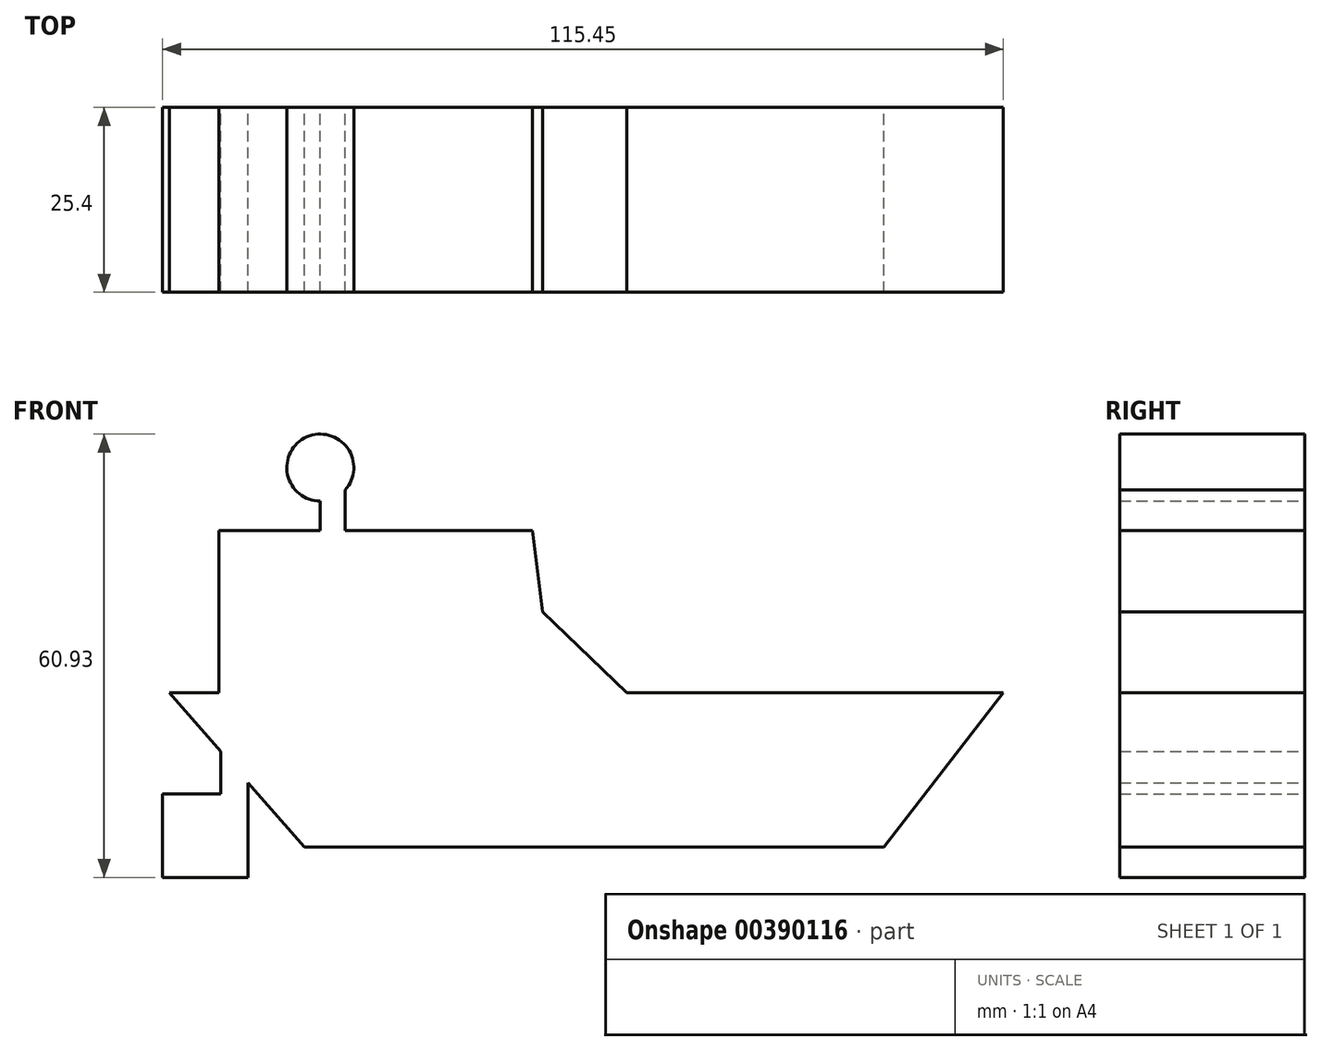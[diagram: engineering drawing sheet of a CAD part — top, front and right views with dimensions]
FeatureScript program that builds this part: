
annotation { "Feature Type Name" : "Feature", "Feature Type Description" : "" }
export const myFeature = defineFeature(function(context is Context, id is Id, definition is map)
    precondition{}
    {
        {
            var Q0;
            Q0=qCreatedBy(makeId("Front.planeOp"),FACE);
            var sketch = newSketch(context, id + "F0", { "sketchPlane" : qUnion([Q0])});
            skLineSegment(sketch, "E0", {"start": v(-56.02, 21.2) * mm, "end": v(-37.45, 0) * mm});
            skLineSegment(sketch, "E1", {"start": v(-37.45, 0) * mm, "end": v(42.1, 0) * mm});
            skLineSegment(sketch, "E2", {"start": v(42.1, 0) * mm, "end": v(58.5, 21.2) * mm});
            skLineSegment(sketch, "E3", {"start": v(58.5, 21.2) * mm, "end": v(-56.02, 21.2) * mm});
            skLineSegment(sketch, "E4", {"start": v(-3.4, 21.2) * mm, "end": v(-49.21, 21.2) * mm});
            skLineSegment(sketch, "E5", {"start": v(-49.21, 21.2) * mm, "end": v(-49.21, 43.49) * mm});
            skLineSegment(sketch, "E6", {"start": v(-49.21, 43.49) * mm, "end": v(-6.2, 43.49) * mm});
            skLineSegment(sketch, "E7", {"start": v(-6.2, 43.49) * mm, "end": v(-3.4, 21.2) * mm});
            skLineSegment(sketch, "E8", {"start": v(-4.8, 32.34) * mm, "end": v(6.8, 21.2) * mm});
            skLineSegment(sketch, "E9", {"start": v(-48.94, 13.12) * mm, "end": v(-48.94, 7.27) * mm});
            skLineSegment(sketch, "E10", {"start": v(-48.94, 7.27) * mm, "end": v(-56.95, 7.27) * mm});
            skLineSegment(sketch, "E11", {"start": v(-56.95, 7.27) * mm, "end": v(-56.95, -4.18) * mm});
            skLineSegment(sketch, "E12", {"start": v(-56.95, -4.18) * mm, "end": v(-45.19, -4.18) * mm});
            skLineSegment(sketch, "E13", {"start": v(-45.19, -4.18) * mm, "end": v(-45.19, 8.83) * mm});
            skLineSegment(sketch, "E14", {"start": v(-35.28, 43.49) * mm, "end": v(-31.88, 43.49) * mm});
            skLineSegment(sketch, "E15", {"start": v(-31.88, 43.49) * mm, "end": v(-31.88, 52.15) * mm});
            skLineSegment(sketch, "E16", {"start": v(-31.88, 52.15) * mm, "end": v(-35.28, 52.15) * mm});
            skLineSegment(sketch, "E17", {"start": v(-35.28, 52.15) * mm, "end": v(-35.28, 43.49) * mm});
            skCircle(sketch, "E18", {"center": v(-35.28, 52.15) * mm, "radius": 4.6 * mm});
            skSolve(sketch);
        }
        {
            var Q0;
            Q0 = qSketchRegion(id + "F0", true);
            extrude(context, id + "F1", {"entities" : qUnion([Q0]), "depth" : 25.4 * mm});
        }
    });
